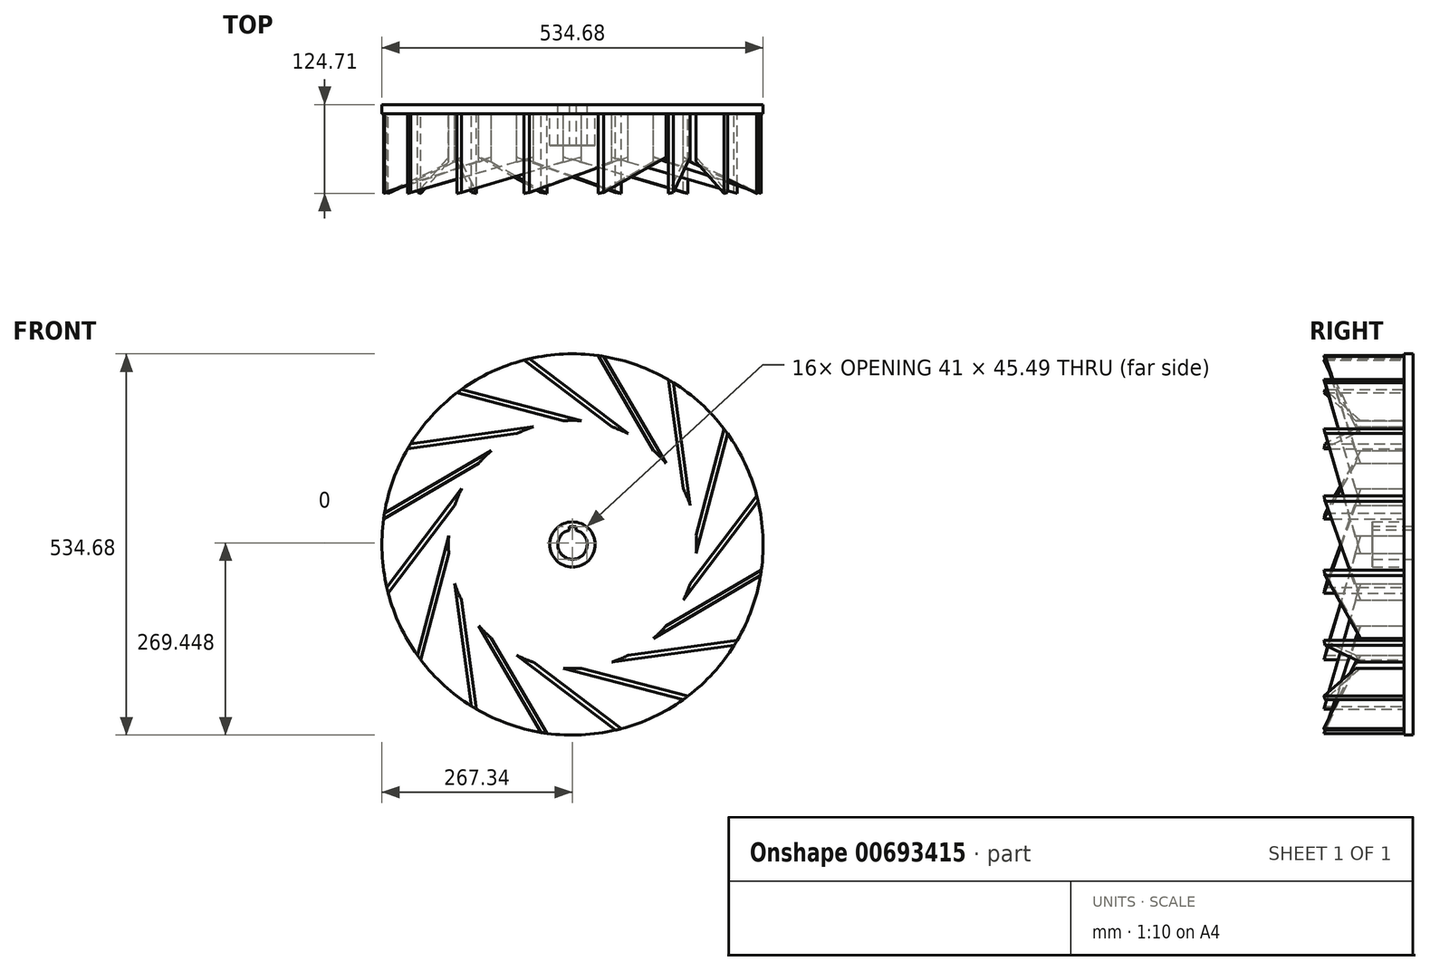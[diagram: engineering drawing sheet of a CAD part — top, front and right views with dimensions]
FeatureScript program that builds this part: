
annotation { "Feature Type Name" : "Feature", "Feature Type Description" : "" }
export const myFeature = defineFeature(function(context is Context, id is Id, definition is map)
    precondition{}
    {
        {
            var Q0;
            Q0=qCreatedBy(makeId("Front.planeOp"),FACE);
            var sketch = newSketch(context, id + "F0", { "sketchPlane" : qUnion([Q0])});
            skCircle(sketch, "E0", {"center": v(0, 0) * mm, "radius": 267.34 * mm});
            skCircle(sketch, "E1", {"center": v(0, 0) * mm, "radius": 20.64 * mm});
            skLineSegment(sketch, "E2", {"start": v(-20.64, -20.64) * mm, "end": v(20.64, -20.64) * mm, "construction": true});
            skPoint(sketch, "E3", {"position": v(0, -20.64) * mm});
            skSolve(sketch);
        }
        {
            var Q0;
            Q0=makeQuery(id+"F0.imprint","IMPRINT",FACE,{"disambiguationData":[TD([[makeQuery(id+"F0.imprint","IMPRINT",EDGE,{"derivedFrom":sQuery(id+"F0.wireOp",EDGE,"E0")}),1.0]])]});
            extrude(context, id + "F1", {"entities" : qUnion([Q0]), "depth" : 12.7 * mm, "offsetDistance" : 25.4 * mm});
        }
        {
            var Q0;
            Q0=makeQuery(id+"F1.opExtrude","CAP_FACE",FACE,{"disambiguationData":[OSD([sQuery(id+"F0.wireOp",EDGE,"E0"),sQuery(id+"F0.wireOp",EDGE,"E1"),sQuery(id+"F0.wireOp",EDGE,"22z9Mpfb-dNJj-jGWx-kTEE-og0KnYas9VtR.bottom"),sQuery(id+"F0.wireOp",EDGE,"22z9Mpfb-dNJj-jGWx-kTEE-og0KnYas9VtR.left"),sQuery(id+"F0.wireOp",EDGE,"22z9Mpfb-dNJj-jGWx-kTEE-og0KnYas9VtR.right")])],"isStart":false});
            var sketch = newSketch(context, id + "F2", { "sketchPlane" : qUnion([Q0])});
            skCircle(sketch, "E4", {"center": v(0, 0) * mm, "radius": 174 * mm, "construction": true});
            skLineSegment(sketch, "E5", {"start": v(-12.55, 173.54) * mm, "end": v(-162.02, 212.64) * mm});
            skLineSegment(sketch, "E6", {"start": v(12.55, 173.54) * mm, "end": v(-155.46, 217.49) * mm});
            skLineSegment(sketch, "E7", {"start": v(-12.55, 173.54) * mm, "end": v(12.55, 173.54) * mm, "construction": true});
            skArc(sketch, "E8", {"start": v(12.55, 173.54) * mm, "mid": v(0, 173.99) * mm, "end": v(-12.55, 173.54) * mm});
            skLineSegment(sketch, "E9", {"start": v(0, 0) * mm, "end": v(142.6, 0) * mm, "construction": true});
            skCircle(sketch, "E10", {"center": v(0, 0) * mm, "radius": 31.75 * mm});
            skSolve(sketch);
        }
        {
            var Q0;
            {var subQ5=sQuery(id+"F2.wireOp",EDGE,"E6");Q0=makeQuery(id+"F2.imprint","IMPRINT",FACE,{"disambiguationData":[TD([[makeQuery(id+"F2.imprint","IMPRINT",EDGE,{"derivedFrom":subQ5}),1.0]])]});}
            var Q1;
            Q1=makeQuery(id+"F2.imprint","IMPRINT",FACE,{"disambiguationData":[TD([[makeQuery(id+"F2.imprint","IMPRINT",EDGE,{"derivedFrom":sQuery(id+"F2.wireOp",EDGE,"7mRhA2gL-O8xT-6R13-JbKQ-co5Zex9MbeP1")}),-1.0]])]});
            extrude(context, id + "F3", {"entities" : qUnion([Q0, Q1]), "operationType" : NewBodyOperationType.ADD, "depth" : 241.3 * mm, "offsetDistance" : 25.4 * mm});
        }
        {
            var Q0;
            Q0=makeQuery(id+"F2.imprint","IMPRINT",FACE,{"disambiguationData":[TD([[makeQuery(id+"F2.imprint","IMPRINT",EDGE,{"derivedFrom":sQuery(id+"F2.wireOp",EDGE,"E10")}),1.0]])]});
            extrude(context, id + "F4", {"entities" : qUnion([Q0]), "operationType" : NewBodyOperationType.ADD, "depth" : 44.45 * mm, "offsetDistance" : 25.4 * mm});
        }
        {
            var Q0;
            Q0=makeQuery(id+"F3.opExtrude","SWEPT_FACE",FACE,{"disambiguationData":[OSD([sQuery(id+"F2.wireOp",EDGE,"E6")])]});
            var sketch = newSketch(context, id + "F5", { "sketchPlane" : qUnion([Q0])});
            skLineSegment(sketch, "E11.0", {"start": v(-210.57, -254) * mm, "end": v(-210.57, -124.71) * mm});
            skLineSegment(sketch, "E12.0", {"start": v(-205.44, -254) * mm, "end": v(-210.57, -254) * mm});
            skLineSegment(sketch, "E13.0", {"start": v(-31.78, -254) * mm, "end": v(-205.44, -254) * mm});
            skLineSegment(sketch, "E14.0", {"start": v(-31.78, -254) * mm, "end": v(-31.78, -73.66) * mm});
            skLineSegment(sketch, "E15", {"start": v(-31.78, -73.66) * mm, "end": v(-210.57, -124.71) * mm});
            skPoint(sketch, "E16.orphan", {"position": v(-31.78, -12.7) * mm});
            skPoint(sketch, "E17.orphan", {"position": v(-210.57, -12.7) * mm});
            skSolve(sketch);
        }
        {
            var Q0;
            Q0=qCreatedBy(makeId("Right.planeOp"),FACE);
            var sketch = newSketch(context, id + "F6", { "sketchPlane" : qUnion([Q0])});
            skLineSegment(sketch, "E18", {"start": v(65.01, 0) * mm, "end": v(-215.97, 0) * mm, "construction": true});
            skSolve(sketch);
        }
        {
            var Q0;
            {var subQ0=sQuery(id+"F5.wireOp",EDGE,"E13.0");Q0=makeQuery(id+"F5.imprint","IMPRINT",FACE,{"disambiguationData":[TD([[makeQuery(id+"F5.imprint","IMPRINT",EDGE,{"derivedFrom":subQ0}),-1.0]])]});}
            var Q1;
            {var subQ0=sQuery(id+"F5.wireOp",EDGE,"E11.0");Q1=makeQuery(id+"F5.imprint","IMPRINT",FACE,{"disambiguationData":[TD([[makeQuery(id+"F5.imprint","IMPRINT",EDGE,{"derivedFrom":subQ0}),-1.0]])]});}
            extrude(context, id + "F7", {"entities" : qUnion([Q0, Q1]), "operationType" : NewBodyOperationType.REMOVE, "endBound" : BoundingType.UP_TO_NEXT, "oppositeDirection" : true, "depth" : 25.4 * mm, "offsetDistance" : 25.4 * mm});
        }
        {
            var Q0;
            Q0=makeQuery(id+"F1.opExtrude","SWEPT_BODY",BODY,{"disambiguationData":[OSD([sQuery(id+"F0.wireOp",EDGE,"E0"),sQuery(id+"F0.wireOp",EDGE,"E1"),sQuery(id+"F0.wireOp",EDGE,"22z9Mpfb-dNJj-jGWx-kTEE-og0KnYas9VtR.bottom"),sQuery(id+"F0.wireOp",EDGE,"22z9Mpfb-dNJj-jGWx-kTEE-og0KnYas9VtR.left"),sQuery(id+"F0.wireOp",EDGE,"22z9Mpfb-dNJj-jGWx-kTEE-og0KnYas9VtR.right")])]});
            var Q1;
            Q1=sQuery(id+"F6.wireOp",EDGE,"E18");
            circularPattern(context, id + "F8", {"entities" : qUnion([Q0]), "axis" : qUnion([Q1]), "angle" : 360 * degree, "instanceCount" : 16, "equalSpace" : true});
        }
        {
            var Q0;
            Q0=makeQuery(id+"F4.opExtrude","CAP_FACE",FACE,{"disambiguationData":[OSD([sQuery(id+"F0.wireOp",EDGE,"E1"),sQuery(id+"F2.wireOp",EDGE,"E10")])],"isStart":false});
            var sketch = newSketch(context, id + "F9", { "sketchPlane" : qUnion([Q0])});
            skLineSegment(sketch, "E19.bottom", {"start": v(-4.76, 15.33) * mm, "end": v(4.76, 15.33) * mm});
            skLineSegment(sketch, "E19.top", {"start": v(-4.76, 24.85) * mm, "end": v(4.76, 24.85) * mm});
            skLineSegment(sketch, "E19.left", {"start": v(-4.76, 15.33) * mm, "end": v(-4.76, 24.85) * mm});
            skLineSegment(sketch, "E19.right", {"start": v(4.76, 15.33) * mm, "end": v(4.76, 24.85) * mm});
            skCircle(sketch, "E20.0", {"center": v(0, 0) * mm, "radius": 20.64 * mm, "construction": true});
            skLineSegment(sketch, "E21", {"start": v(-20.64, -20.64) * mm, "end": v(20.64, -20.64) * mm, "construction": true});
            skPoint(sketch, "E22", {"position": v(0, -20.64) * mm});
            skSolve(sketch);
        }
        {
            var Q0;
            {var subQ0=sQuery(id+"F9.wireOp",EDGE,"E19.top");Q0=makeQuery(id+"F9.imprint","IMPRINT",FACE,{"disambiguationData":[TD([[makeQuery(id+"F9.imprint","IMPRINT",EDGE,{"derivedFrom":subQ0}),-1.0]])]});}
            extrude(context, id + "F10", {"entities" : qUnion([Q0]), "operationType" : NewBodyOperationType.REMOVE, "endBound" : BoundingType.UP_TO_NEXT, "oppositeDirection" : true, "depth" : 25.4 * mm, "offsetDistance" : 25.4 * mm});
        }
    });
